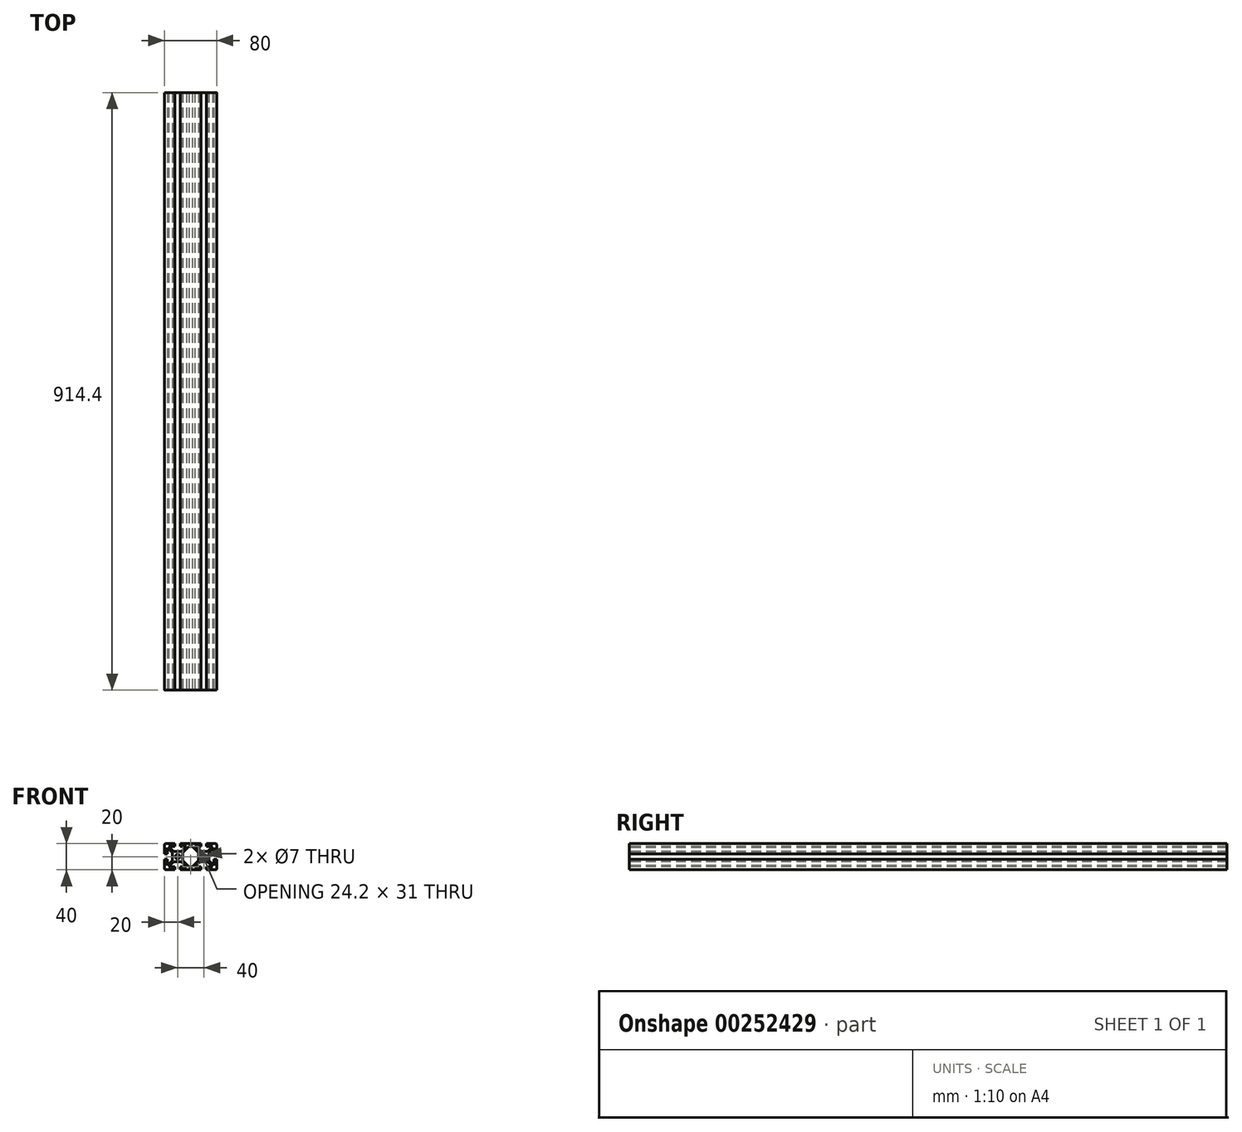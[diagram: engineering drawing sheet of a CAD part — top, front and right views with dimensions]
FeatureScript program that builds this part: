
annotation { "Feature Type Name" : "Feature", "Feature Type Description" : "" }
export const myFeature = defineFeature(function(context is Context, id is Id, definition is map)
    precondition{}
    {
        {
            var Q0;
            Q0=qCreatedBy(makeId("Front.planeOp"),FACE);
            var sketch = newSketch(context, id + "F0", { "sketchPlane" : qUnion([Q0])});
            skLineSegment(sketch, "E0.bottom", {"start": v(-38, 20) * mm, "end": v(-24, 20) * mm});
            skLineSegment(sketch, "E0.top", {"start": v(-38, -20) * mm, "end": v(-24, -20) * mm});
            skLineSegment(sketch, "E0.left", {"start": v(-40, 18) * mm, "end": v(-40, 4) * mm});
            skLineSegment(sketch, "E0.right", {"start": v(40, 18) * mm, "end": v(40, 4) * mm});
            skPoint(sketch, "E0.middle", {"position": v(0, 0) * mm});
            skCircle(sketch, "E1", {"center": v(-20, 0) * mm, "radius": 3.5 * mm});
            skCircle(sketch, "E2", {"center": v(20, 0) * mm, "radius": 3.5 * mm});
            skLineSegment(sketch, "E3.0", {"start": v(-33.54, 15.5) * mm, "end": v(-24, 15.5) * mm});
            skLineSegment(sketch, "E3.1", {"start": v(-35.5, 13.54) * mm, "end": v(-35.5, 4) * mm});
            skLineSegment(sketch, "E3.2", {"start": v(-33.54, -15.5) * mm, "end": v(-24, -15.5) * mm});
            skLineSegment(sketch, "E3.3", {"start": v(35.5, 13.54) * mm, "end": v(35.5, 4) * mm});
            skLineSegment(sketch, "E4", {"start": v(-20, 20) * mm, "end": v(-20, -20) * mm, "construction": true});
            skLineSegment(sketch, "E5", {"start": v(-24, 20) * mm, "end": v(-24, 15.5) * mm});
            skLineSegment(sketch, "E6", {"start": v(-16, 20) * mm, "end": v(-16, 15.5) * mm});
            skLineSegment(sketch, "E7", {"start": v(16, 20) * mm, "end": v(16, 15.5) * mm});
            skLineSegment(sketch, "E8", {"start": v(24, 20) * mm, "end": v(24, 15.5) * mm});
            skLineSegment(sketch, "E9.MirrorCS", {"start": v(-24, -20) * mm, "end": v(-24, -15.5) * mm});
            skLineSegment(sketch, "E10.MirrorCS", {"start": v(-16, -20) * mm, "end": v(-16, -15.5) * mm});
            skLineSegment(sketch, "E11.MirrorCS", {"start": v(16, -20) * mm, "end": v(16, -15.5) * mm});
            skLineSegment(sketch, "E12.MirrorCS", {"start": v(24, -20) * mm, "end": v(24, -15.5) * mm});
            skLineSegment(sketch, "E13", {"start": v(-40, 4) * mm, "end": v(-35.5, 4) * mm});
            skLineSegment(sketch, "E14", {"start": v(-40, -4) * mm, "end": v(-35.5, -4) * mm});
            skLineSegment(sketch, "E15.MirrorCS", {"start": v(40, 4) * mm, "end": v(35.5, 4) * mm});
            skLineSegment(sketch, "E16.MirrorCS", {"start": v(40, -4) * mm, "end": v(35.5, -4) * mm});
            skLineSegment(sketch, "E17.trimOffspring", {"start": v(-35.5, -4) * mm, "end": v(-35.5, -13.54) * mm});
            skLineSegment(sketch, "E18.trimOffspring", {"start": v(-40, -4) * mm, "end": v(-40, -18) * mm});
            skLineSegment(sketch, "E19.trimOffspring", {"start": v(-16, 20) * mm, "end": v(16, 20) * mm});
            skLineSegment(sketch, "E20.trimOffspring", {"start": v(-16, 15.5) * mm, "end": v(-6.46, 15.5) * mm});
            skLineSegment(sketch, "E21.trimOffspring", {"start": v(24, 20) * mm, "end": v(38, 20) * mm});
            skLineSegment(sketch, "E22.trimOffspring", {"start": v(24, 15.5) * mm, "end": v(33.54, 15.5) * mm});
            skLineSegment(sketch, "E23.trimOffspring", {"start": v(35.5, -4) * mm, "end": v(35.5, -13.54) * mm});
            skLineSegment(sketch, "E24.trimOffspring", {"start": v(40, -4) * mm, "end": v(40, -18) * mm});
            skLineSegment(sketch, "E25.trimOffspring", {"start": v(-16, -15.5) * mm, "end": v(-6.46, -15.5) * mm});
            skLineSegment(sketch, "E26.trimOffspring", {"start": v(-16, -20) * mm, "end": v(16, -20) * mm});
            skLineSegment(sketch, "E27.trimOffspring", {"start": v(24, -15.5) * mm, "end": v(33.54, -15.5) * mm});
            skLineSegment(sketch, "E28.trimOffspring", {"start": v(24, -20) * mm, "end": v(38, -20) * mm});
            skLineSegment(sketch, "E29", {"start": v(-33.54, 15.5) * mm, "end": v(-25.94, 7.9) * mm});
            skLineSegment(sketch, "E30.MirrorCS", {"start": v(-35.5, 13.54) * mm, "end": v(-27.9, 5.94) * mm});
            skLineSegment(sketch, "E31.MirrorCS", {"start": v(-35.5, -13.54) * mm, "end": v(-27.9, -5.94) * mm});
            skLineSegment(sketch, "E32.MirrorCS", {"start": v(-33.54, -15.5) * mm, "end": v(-25.94, -7.9) * mm});
            skLineSegment(sketch, "E33.MirrorCS", {"start": v(-6.46, 15.5) * mm, "end": v(-14.06, 7.9) * mm});
            skLineSegment(sketch, "E34.MirrorCS", {"start": v(-2.54, 15.5) * mm, "end": v(-12.1, 5.94) * mm});
            skLineSegment(sketch, "E35.MirrorCS", {"start": v(-2.54, -15.5) * mm, "end": v(-12.1, -5.94) * mm});
            skLineSegment(sketch, "E36.MirrorCS", {"start": v(-6.46, -15.5) * mm, "end": v(-14.06, -7.9) * mm});
            skLineSegment(sketch, "E37.MirrorCS", {"start": v(2.54, 15.5) * mm, "end": v(12.1, 5.94) * mm});
            skLineSegment(sketch, "E38.MirrorCS", {"start": v(6.46, 15.5) * mm, "end": v(14.06, 7.9) * mm});
            skLineSegment(sketch, "E39.MirrorCS", {"start": v(33.54, 15.5) * mm, "end": v(25.94, 7.9) * mm});
            skLineSegment(sketch, "E40.MirrorCS", {"start": v(35.5, 13.54) * mm, "end": v(27.9, 5.94) * mm});
            skLineSegment(sketch, "E41.MirrorCS", {"start": v(35.5, -13.54) * mm, "end": v(27.9, -5.94) * mm});
            skLineSegment(sketch, "E42.MirrorCS", {"start": v(33.54, -15.5) * mm, "end": v(25.94, -7.9) * mm});
            skLineSegment(sketch, "E43.MirrorCS", {"start": v(6.46, -15.5) * mm, "end": v(14.06, -7.9) * mm});
            skLineSegment(sketch, "E44.MirrorCS", {"start": v(2.54, -15.5) * mm, "end": v(12.1, -5.94) * mm});
            skLineSegment(sketch, "E45", {"start": v(-25.94, 7.9) * mm, "end": v(-14.06, 7.9) * mm});
            skLineSegment(sketch, "E46", {"start": v(14.06, 7.9) * mm, "end": v(25.94, 7.9) * mm});
            skLineSegment(sketch, "E47", {"start": v(27.9, 5.94) * mm, "end": v(27.9, -5.94) * mm});
            skLineSegment(sketch, "E48", {"start": v(25.94, -7.9) * mm, "end": v(14.06, -7.9) * mm});
            skLineSegment(sketch, "E49", {"start": v(-27.9, 5.94) * mm, "end": v(-27.9, -5.94) * mm});
            skLineSegment(sketch, "E50", {"start": v(-25.94, -7.9) * mm, "end": v(-14.06, -7.9) * mm});
            skLineSegment(sketch, "E51", {"start": v(-12.1, 5.94) * mm, "end": v(-12.1, -5.94) * mm});
            skLineSegment(sketch, "E52", {"start": v(12.1, 5.94) * mm, "end": v(12.1, -5.94) * mm});
            skLineSegment(sketch, "E53.trimOffspring", {"start": v(-2.54, 15.5) * mm, "end": v(2.54, 15.5) * mm});
            skLineSegment(sketch, "E54.trimOffspring", {"start": v(6.46, 15.5) * mm, "end": v(16, 15.5) * mm});
            skLineSegment(sketch, "E55.trimOffspring", {"start": v(-2.54, -15.5) * mm, "end": v(2.54, -15.5) * mm});
            skLineSegment(sketch, "E56.trimOffspring", {"start": v(6.46, -15.5) * mm, "end": v(16, -15.5) * mm});
            skPoint(sketch, "E57.visualSharp", {"position": v(-40, 20) * mm});
            skArc(sketch, "E57.filletArc", {"start": v(-38, 20) * mm, "mid": v(-39.41, 19.41) * mm, "end": v(-40, 18) * mm});
            skPoint(sketch, "E58.visualSharp", {"position": v(-40, -20) * mm});
            skArc(sketch, "E58.filletArc", {"start": v(-40, -18) * mm, "mid": v(-39.41, -19.41) * mm, "end": v(-38, -20) * mm});
            skPoint(sketch, "E59.visualSharp", {"position": v(40, 20) * mm});
            skArc(sketch, "E59.filletArc", {"start": v(40, 18) * mm, "mid": v(39.41, 19.41) * mm, "end": v(38, 20) * mm});
            skPoint(sketch, "E60.visualSharp", {"position": v(40, -20) * mm});
            skArc(sketch, "E60.filletArc", {"start": v(38, -20) * mm, "mid": v(39.41, -19.41) * mm, "end": v(40, -18) * mm});
            skSolve(sketch);
        }
        {
            var Q0;
            Q0=makeQuery(id+"F0.imprint","IMPRINT",FACE,{"disambiguationData":[TD([[makeQuery(id+"F0.imprint","IMPRINT",EDGE,{"derivedFrom":sQuery(id+"F0.wireOp",EDGE,"E0.bottom")}),-1.0]])]});
            var Q1;
            Q1=makeQuery(id+"F0.imprint","IMPRINT",FACE,{"disambiguationData":[TD([[makeQuery(id+"F0.imprint","IMPRINT",EDGE,{"derivedFrom":sQuery(id+"F0.wireOp",EDGE,"E0.right")}),-1.0]])]});
            extrude(context, id + "F1", {"entities" : qUnion([Q0, Q1]), "oppositeDirection" : true, "depth" : 914.4 * mm});
        }
    });
